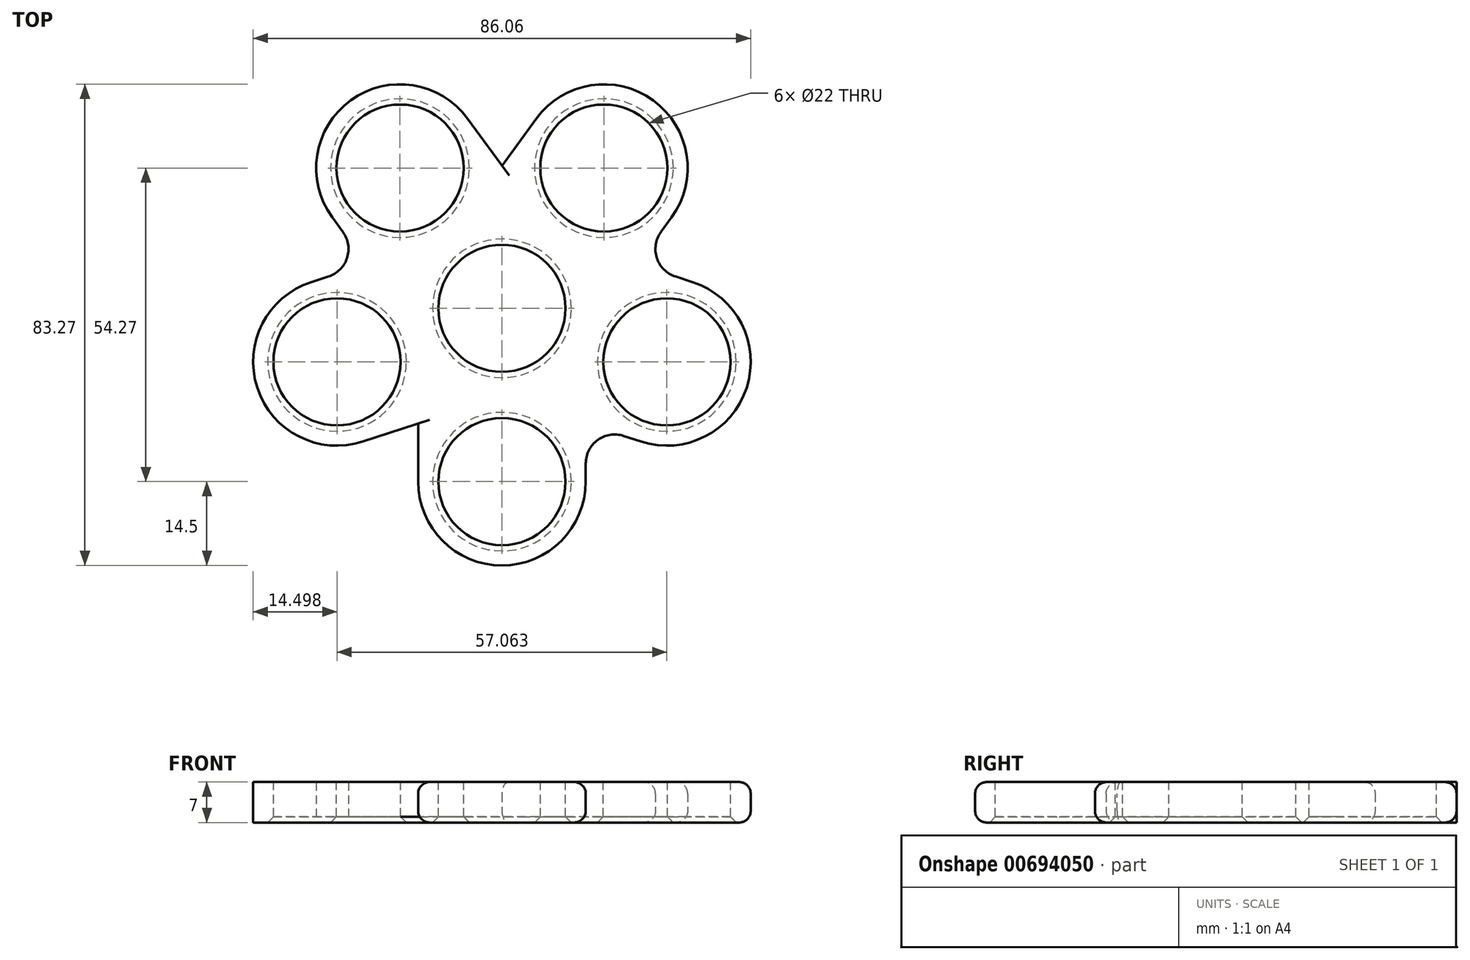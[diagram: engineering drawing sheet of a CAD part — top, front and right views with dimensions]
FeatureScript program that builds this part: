
annotation { "Feature Type Name" : "Feature", "Feature Type Description" : "" }
export const myFeature = defineFeature(function(context is Context, id is Id, definition is map)
    precondition{}
    {
        {
            var Q0;
            Q0=qCreatedBy(makeId("Top.planeOp"),FACE);
            var sketch = newSketch(context, id + "F0", { "sketchPlane" : qUnion([Q0])});
            skCircle(sketch, "E0", {"center": v(0, 0) * mm, "radius": 14.5 * mm});
            skCircle(sketch, "E1", {"center": v(0, -30) * mm, "radius": 14.5 * mm});
            skLineSegment(sketch, "E2", {"start": v(14.5, 0) * mm, "end": v(14.5, -30) * mm});
            skLineSegment(sketch, "E3", {"start": v(-14.5, 0) * mm, "end": v(-14.5, -30) * mm});
            skSolve(sketch);
        }
        {
            var Q0;
            Q0=qSketchRegion(id+"F0",true);
            var Q1;
            {var subQ0=sQuery(id+"F0.wireOp",EDGE,"E1");var subQ1=sQuery(id+"F0.wireOp",EDGE,"E0");var subQ2=makeQuery(id+"F0.imprint","INTERSECT",VERTEX,{"disambiguationData":[OD(0.0)],"derivedFrom":[subQ1,subQ0]});Q1=makeQuery(id+"F0.imprint","IMPRINT",FACE,{"disambiguationData":[TD([[makeQuery(id+"F0.imprint","IMPRINT",EDGE,{"disambiguationData":[TD([[subQ2,-1.0]])],"derivedFrom":subQ1}),1.0]])]});}
            extrude(context, id + "F1", {"entities" : qUnion([Q0, Q1]), "depth" : 7 * mm, "offsetDistance" : 25 * mm});
        }
        {
            var Q0;
            Q0=makeQuery(id+"F1.opExtrude","CAP_FACE",FACE,{"disambiguationData":[OSD([sQuery(id+"F0.wireOp",EDGE,"E0"),sQuery(id+"F0.wireOp",EDGE,"E1"),sQuery(id+"F0.wireOp",EDGE,"E2"),sQuery(id+"F0.wireOp",EDGE,"E3")])],"isStart":false});
            var sketch = newSketch(context, id + "F2", { "sketchPlane" : qUnion([Q0])});
            skCircle(sketch, "E4", {"center": v(0, 0) * mm, "radius": 11 * mm});
            skCircle(sketch, "E5", {"center": v(0, -30) * mm, "radius": 11 * mm});
            skLineSegment(sketch, "E6", {"start": v(0, 0) * mm, "end": v(0, -30) * mm});
            skSolve(sketch);
        }
        {
            var Q0;
            Q0=qSketchRegion(id+"F2",true);
            extrude(context, id + "F3", {"entities" : qUnion([Q0]), "operationType" : NewBodyOperationType.REMOVE, "endBound" : BoundingType.THROUGH_ALL, "oppositeDirection" : true, "depth" : 25 * mm, "offsetDistance" : 25 * mm});
        }
        {
            var Q0;
            Q0=qCreatedBy(makeId("Front.planeOp"),FACE);
            var sketch = newSketch(context, id + "F4", { "sketchPlane" : qUnion([Q0])});
            skLineSegment(sketch, "E7", {"start": v(0, 0) * mm, "end": v(0, 26.48) * mm});
            skSolve(sketch);
        }
        {
            var Q0;
            Q0=makeQuery(id+"F1.opExtrude","SWEPT_BODY",BODY,{"disambiguationData":[OSD([sQuery(id+"F0.wireOp",EDGE,"E0"),sQuery(id+"F0.wireOp",EDGE,"E1"),sQuery(id+"F0.wireOp",EDGE,"E2"),sQuery(id+"F0.wireOp",EDGE,"E3")])]});
            var Q1;
            Q1=sQuery(id+"F4.wireOp",EDGE,"E7");
            circularPattern(context, id + "F5", {"entities" : qUnion([Q0]), "axis" : qUnion([Q1]), "angle" : 360 * degree, "instanceCount" : 5, "equalSpace" : true});
        }
        {
            var Q0;
            Q0=makeQuery(id+"F5.opPattern","COPY",BODY,{"derivedFrom":makeQuery(id+"F1.opExtrude","SWEPT_BODY",BODY,{"disambiguationData":[OSD([sQuery(id+"F0.wireOp",EDGE,"E0"),sQuery(id+"F0.wireOp",EDGE,"E1"),sQuery(id+"F0.wireOp",EDGE,"E2"),sQuery(id+"F0.wireOp",EDGE,"E3")])]}),"instanceName":"4"});
            var Q1;
            Q1=makeQuery(id+"F5.opPattern","COPY",BODY,{"derivedFrom":makeQuery(id+"F1.opExtrude","SWEPT_BODY",BODY,{"disambiguationData":[OSD([sQuery(id+"F0.wireOp",EDGE,"E0"),sQuery(id+"F0.wireOp",EDGE,"E1"),sQuery(id+"F0.wireOp",EDGE,"E2"),sQuery(id+"F0.wireOp",EDGE,"E3")])]}),"instanceName":"3"});
            var Q2;
            Q2=makeQuery(id+"F5.opPattern","COPY",BODY,{"derivedFrom":makeQuery(id+"F1.opExtrude","SWEPT_BODY",BODY,{"disambiguationData":[OSD([sQuery(id+"F0.wireOp",EDGE,"E0"),sQuery(id+"F0.wireOp",EDGE,"E1"),sQuery(id+"F0.wireOp",EDGE,"E2"),sQuery(id+"F0.wireOp",EDGE,"E3")])]}),"instanceName":"2"});
            var Q3;
            Q3=makeQuery(id+"F5.opPattern","COPY",BODY,{"derivedFrom":makeQuery(id+"F1.opExtrude","SWEPT_BODY",BODY,{"disambiguationData":[OSD([sQuery(id+"F0.wireOp",EDGE,"E0"),sQuery(id+"F0.wireOp",EDGE,"E1"),sQuery(id+"F0.wireOp",EDGE,"E2"),sQuery(id+"F0.wireOp",EDGE,"E3")])]}),"instanceName":"1"});
            var Q4;
            Q4=makeQuery(id+"F1.opExtrude","SWEPT_BODY",BODY,{"disambiguationData":[OSD([sQuery(id+"F0.wireOp",EDGE,"E0"),sQuery(id+"F0.wireOp",EDGE,"E1"),sQuery(id+"F0.wireOp",EDGE,"E2"),sQuery(id+"F0.wireOp",EDGE,"E3")])]});
            var Q5;
            Q5=makeQuery(id+"F5.opPattern","COPY",BODY,{"derivedFrom":makeQuery(id+"F1.opExtrude","SWEPT_BODY",BODY,{"disambiguationData":[OSD([sQuery(id+"F0.wireOp",EDGE,"E0"),sQuery(id+"F0.wireOp",EDGE,"E1"),sQuery(id+"F0.wireOp",EDGE,"E2"),sQuery(id+"F0.wireOp",EDGE,"E3")])]}),"instanceName":"5"});
            booleanBodies(context, id + "F6", {"operationType" : BooleanOperationType.UNION, "tools" : qUnion([Q0, Q1, Q2, Q3, Q4, Q5])});
        }
        {
            var Q0;
            Q0=makeQuery(id+"F6.opBoolean","INTERSECT",EDGE,{"derivedFrom":[makeQuery(id+"F5.opPattern","COPY",FACE,{"derivedFrom":makeQuery(id+"F1.opExtrude","SWEPT_FACE",FACE,{"disambiguationData":[OSD([sQuery(id+"F0.wireOp",EDGE,"E2")])]}),"instanceName":"4"}),makeQuery(id+"F5.opPattern","COPY",FACE,{"derivedFrom":makeQuery(id+"F1.opExtrude","SWEPT_FACE",FACE,{"disambiguationData":[OSD([sQuery(id+"F0.wireOp",EDGE,"E3")])]}),"instanceName":"5"})]});
            var Q1;
            Q1=makeQuery(id+"F6.opBoolean","INTERSECT",EDGE,{"derivedFrom":[makeQuery(id+"F1.opExtrude","SWEPT_FACE",FACE,{"disambiguationData":[OSD([sQuery(id+"F0.wireOp",EDGE,"E3")])]}),makeQuery(id+"F5.opPattern","COPY",FACE,{"derivedFrom":makeQuery(id+"F1.opExtrude","SWEPT_FACE",FACE,{"disambiguationData":[OSD([sQuery(id+"F0.wireOp",EDGE,"E2")])]}),"instanceName":"5"})]});
            var Q2;
            Q2=makeQuery(id+"F6.opBoolean","INTERSECT",EDGE,{"derivedFrom":[makeQuery(id+"F1.opExtrude","SWEPT_FACE",FACE,{"disambiguationData":[OSD([sQuery(id+"F0.wireOp",EDGE,"E2")])]}),makeQuery(id+"F5.opPattern","COPY",FACE,{"derivedFrom":makeQuery(id+"F1.opExtrude","SWEPT_FACE",FACE,{"disambiguationData":[OSD([sQuery(id+"F0.wireOp",EDGE,"E3")])]}),"instanceName":"1"})]});
            var Q3;
            Q3=makeQuery(id+"F6.opBoolean","INTERSECT",EDGE,{"derivedFrom":[makeQuery(id+"F5.opPattern","COPY",FACE,{"derivedFrom":makeQuery(id+"F1.opExtrude","SWEPT_FACE",FACE,{"disambiguationData":[OSD([sQuery(id+"F0.wireOp",EDGE,"E2")])]}),"instanceName":"1"}),makeQuery(id+"F5.opPattern","COPY",FACE,{"derivedFrom":makeQuery(id+"F1.opExtrude","SWEPT_FACE",FACE,{"disambiguationData":[OSD([sQuery(id+"F0.wireOp",EDGE,"E3")])]}),"instanceName":"2"})]});
            var Q4;
            {var subQ0=makeQuery(id+"F1.opExtrude","SWEPT_FACE",FACE,{"disambiguationData":[OSD([sQuery(id+"F0.wireOp",EDGE,"E3")])]});Q4=makeQuery(id+"F6.opBoolean","INTERSECT",EDGE,{"derivedFrom":[makeQuery(id+"F5.opPattern","COPY",FACE,{"derivedFrom":subQ0,"instanceName":"3"}),makeQuery(id+"F5.opPattern","COPY",FACE,{"derivedFrom":subQ0,"instanceName":"5"})]});}
            var Q5;
            Q5=makeQuery(id+"F6.opBoolean","INTERSECT",EDGE,{"derivedFrom":[makeQuery(id+"F5.opPattern","COPY",FACE,{"derivedFrom":makeQuery(id+"F1.opExtrude","SWEPT_FACE",FACE,{"disambiguationData":[OSD([sQuery(id+"F0.wireOp",EDGE,"E2")])]}),"instanceName":"3"}),makeQuery(id+"F5.opPattern","COPY",FACE,{"derivedFrom":makeQuery(id+"F1.opExtrude","SWEPT_FACE",FACE,{"disambiguationData":[OSD([sQuery(id+"F0.wireOp",EDGE,"E3")])]}),"instanceName":"4"})]});
            fillet(context, id + "F7", {"entities" : qUnion([Q0, Q1, Q2, Q3, Q4, Q5]), "radius" : 5 * mm, "tangentPropagation" : true, "allowEdgeOverflow" : false});
        }
        {
            var Q0;
            Q0=makeQuery(id+"F5.opPattern","COPY",EDGE,{"derivedFrom":makeQuery(id+"F1.opExtrude","CAP_EDGE",EDGE,{"disambiguationData":[OSD([sQuery(id+"F0.wireOp",EDGE,"E1")])],"isStart":false}),"instanceName":"1"});
            var Q1;
            Q1=makeQuery(id+"F1.opExtrude","CAP_EDGE",EDGE,{"disambiguationData":[OSD([sQuery(id+"F0.wireOp",EDGE,"E1")])],"isStart":true});
            fillet(context, id + "F8", {"entities" : qUnion([Q0, Q1]), "radius" : 2 * mm, "tangentPropagation" : true, "allowEdgeOverflow" : false});
        }
        {
            var Q0;
            Q0=makeQuery(id+"F5.opPattern","COPY",EDGE,{"derivedFrom":makeQuery(id+"F3.boolean.opBoolean","COPY",EDGE,{"derivedFrom":makeQuery(id+"F3.opExtrude","CAP_EDGE",EDGE,{"disambiguationData":[OSD([sQuery(id+"F2.wireOp",EDGE,"E4")])],"isStart":true})}),"instanceName":"4"});
            var Q1;
            Q1=makeQuery(id+"F5.opPattern","COPY",EDGE,{"derivedFrom":makeQuery(id+"F3.boolean.opBoolean","COPY",EDGE,{"derivedFrom":makeQuery(id+"F3.opExtrude","CAP_EDGE",EDGE,{"disambiguationData":[OSD([sQuery(id+"F2.wireOp",EDGE,"E5")])],"isStart":true})}),"instanceName":"2"});
            var Q2;
            Q2=makeQuery(id+"F5.opPattern","COPY",EDGE,{"derivedFrom":makeQuery(id+"F3.boolean.opBoolean","COPY",EDGE,{"derivedFrom":makeQuery(id+"F3.opExtrude","CAP_EDGE",EDGE,{"disambiguationData":[OSD([sQuery(id+"F2.wireOp",EDGE,"E5")])],"isStart":true})}),"instanceName":"3"});
            var Q3;
            Q3=makeQuery(id+"F5.opPattern","COPY",EDGE,{"derivedFrom":makeQuery(id+"F3.boolean.opBoolean","COPY",EDGE,{"derivedFrom":makeQuery(id+"F3.opExtrude","CAP_EDGE",EDGE,{"disambiguationData":[OSD([sQuery(id+"F2.wireOp",EDGE,"E5")])],"isStart":true})}),"instanceName":"4"});
            var Q4;
            Q4=makeQuery(id+"F5.opPattern","COPY",EDGE,{"derivedFrom":makeQuery(id+"F3.boolean.opBoolean","COPY",EDGE,{"derivedFrom":makeQuery(id+"F3.opExtrude","CAP_EDGE",EDGE,{"disambiguationData":[OSD([sQuery(id+"F2.wireOp",EDGE,"E5")])],"isStart":true})}),"instanceName":"5"});
            var Q5;
            Q5=makeQuery(id+"F3.boolean.opBoolean","COPY",EDGE,{"derivedFrom":makeQuery(id+"F3.opExtrude","CAP_EDGE",EDGE,{"disambiguationData":[OSD([sQuery(id+"F2.wireOp",EDGE,"E5")])],"isStart":true})});
            var Q6;
            Q6=makeQuery(id+"F5.opPattern","COPY",EDGE,{"derivedFrom":makeQuery(id+"F3.boolean.opBoolean","COPY",EDGE,{"derivedFrom":makeQuery(id+"F3.opExtrude","CAP_EDGE",EDGE,{"disambiguationData":[OSD([sQuery(id+"F2.wireOp",EDGE,"E5")])],"isStart":true})}),"instanceName":"1"});
            var Q7;
            Q7=makeQuery(id+"F5.opPattern","COPY",EDGE,{"derivedFrom":makeQuery(id+"F3.boolean.opBoolean","INTERSECT",EDGE,{"derivedFrom":[makeQuery(id+"F1.opExtrude","CAP_FACE",FACE,{"disambiguationData":[OSD([sQuery(id+"F0.wireOp",EDGE,"E0"),sQuery(id+"F0.wireOp",EDGE,"E1"),sQuery(id+"F0.wireOp",EDGE,"E2"),sQuery(id+"F0.wireOp",EDGE,"E3")])],"isStart":true}),makeQuery(id+"F3.opExtrude","SWEPT_FACE",FACE,{"disambiguationData":[OSD([sQuery(id+"F2.wireOp",EDGE,"E5")])]})]}),"instanceName":"5"});
            var Q8;
            Q8=makeQuery(id+"F3.boolean.opBoolean","INTERSECT",EDGE,{"derivedFrom":[makeQuery(id+"F1.opExtrude","CAP_FACE",FACE,{"disambiguationData":[OSD([sQuery(id+"F0.wireOp",EDGE,"E0"),sQuery(id+"F0.wireOp",EDGE,"E1"),sQuery(id+"F0.wireOp",EDGE,"E2"),sQuery(id+"F0.wireOp",EDGE,"E3")])],"isStart":true}),makeQuery(id+"F3.opExtrude","SWEPT_FACE",FACE,{"disambiguationData":[OSD([sQuery(id+"F2.wireOp",EDGE,"E5")])]})]});
            var Q9;
            Q9=makeQuery(id+"F5.opPattern","COPY",EDGE,{"derivedFrom":makeQuery(id+"F3.boolean.opBoolean","INTERSECT",EDGE,{"derivedFrom":[makeQuery(id+"F1.opExtrude","CAP_FACE",FACE,{"disambiguationData":[OSD([sQuery(id+"F0.wireOp",EDGE,"E0"),sQuery(id+"F0.wireOp",EDGE,"E1"),sQuery(id+"F0.wireOp",EDGE,"E2"),sQuery(id+"F0.wireOp",EDGE,"E3")])],"isStart":true}),makeQuery(id+"F3.opExtrude","SWEPT_FACE",FACE,{"disambiguationData":[OSD([sQuery(id+"F2.wireOp",EDGE,"E5")])]})]}),"instanceName":"1"});
            var Q10;
            Q10=makeQuery(id+"F5.opPattern","COPY",EDGE,{"derivedFrom":makeQuery(id+"F3.boolean.opBoolean","INTERSECT",EDGE,{"derivedFrom":[makeQuery(id+"F1.opExtrude","CAP_FACE",FACE,{"disambiguationData":[OSD([sQuery(id+"F0.wireOp",EDGE,"E0"),sQuery(id+"F0.wireOp",EDGE,"E1"),sQuery(id+"F0.wireOp",EDGE,"E2"),sQuery(id+"F0.wireOp",EDGE,"E3")])],"isStart":true}),makeQuery(id+"F3.opExtrude","SWEPT_FACE",FACE,{"disambiguationData":[OSD([sQuery(id+"F2.wireOp",EDGE,"E5")])]})]}),"instanceName":"2"});
            var Q11;
            Q11=makeQuery(id+"F5.opPattern","COPY",EDGE,{"derivedFrom":makeQuery(id+"F3.boolean.opBoolean","INTERSECT",EDGE,{"derivedFrom":[makeQuery(id+"F1.opExtrude","CAP_FACE",FACE,{"disambiguationData":[OSD([sQuery(id+"F0.wireOp",EDGE,"E0"),sQuery(id+"F0.wireOp",EDGE,"E1"),sQuery(id+"F0.wireOp",EDGE,"E2"),sQuery(id+"F0.wireOp",EDGE,"E3")])],"isStart":true}),makeQuery(id+"F3.opExtrude","SWEPT_FACE",FACE,{"disambiguationData":[OSD([sQuery(id+"F2.wireOp",EDGE,"E5")])]})]}),"instanceName":"3"});
            var Q12;
            Q12=makeQuery(id+"F5.opPattern","COPY",EDGE,{"derivedFrom":makeQuery(id+"F3.boolean.opBoolean","INTERSECT",EDGE,{"derivedFrom":[makeQuery(id+"F1.opExtrude","CAP_FACE",FACE,{"disambiguationData":[OSD([sQuery(id+"F0.wireOp",EDGE,"E0"),sQuery(id+"F0.wireOp",EDGE,"E1"),sQuery(id+"F0.wireOp",EDGE,"E2"),sQuery(id+"F0.wireOp",EDGE,"E3")])],"isStart":true}),makeQuery(id+"F3.opExtrude","SWEPT_FACE",FACE,{"disambiguationData":[OSD([sQuery(id+"F2.wireOp",EDGE,"E4")])]})]}),"instanceName":"4"});
            var Q13;
            Q13=makeQuery(id+"F5.opPattern","COPY",EDGE,{"derivedFrom":makeQuery(id+"F3.boolean.opBoolean","INTERSECT",EDGE,{"derivedFrom":[makeQuery(id+"F1.opExtrude","CAP_FACE",FACE,{"disambiguationData":[OSD([sQuery(id+"F0.wireOp",EDGE,"E0"),sQuery(id+"F0.wireOp",EDGE,"E1"),sQuery(id+"F0.wireOp",EDGE,"E2"),sQuery(id+"F0.wireOp",EDGE,"E3")])],"isStart":true}),makeQuery(id+"F3.opExtrude","SWEPT_FACE",FACE,{"disambiguationData":[OSD([sQuery(id+"F2.wireOp",EDGE,"E5")])]})]}),"instanceName":"4"});
            chamfer(context, id + "F9", {"entities" : qUnion([Q0, Q1, Q2, Q3, Q4, Q5, Q6, Q7, Q8, Q9, Q10, Q11, Q12, Q13]), "width" : 1 * mm, "tangentPropagation" : true});
        }
    });
